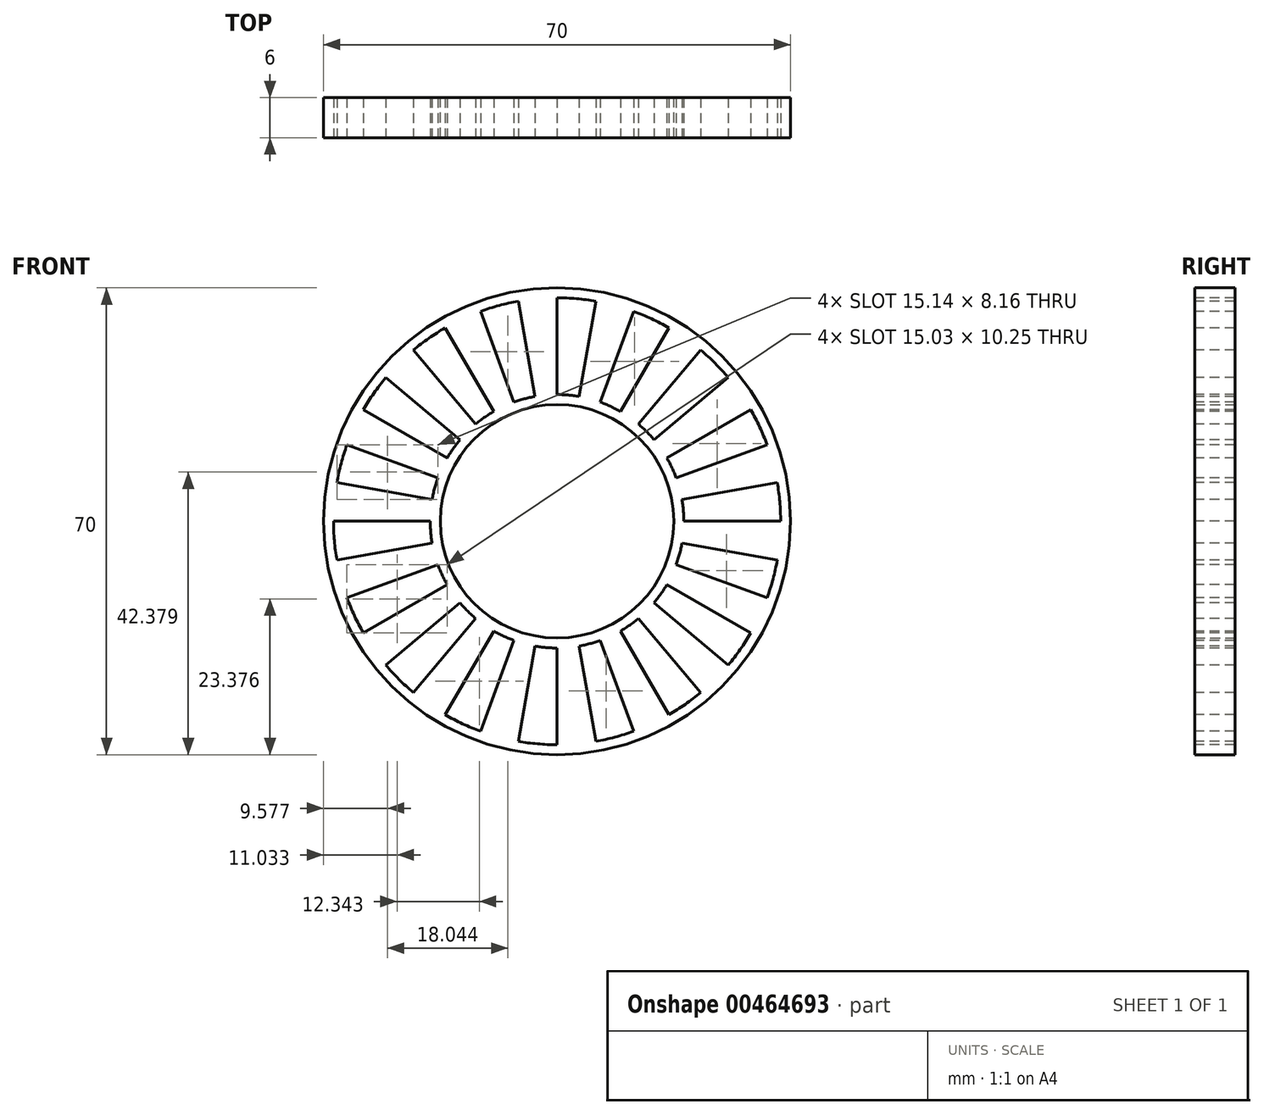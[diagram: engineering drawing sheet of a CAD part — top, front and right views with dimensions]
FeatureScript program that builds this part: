
annotation { "Feature Type Name" : "Feature", "Feature Type Description" : "" }
export const myFeature = defineFeature(function(context is Context, id is Id, definition is map)
    precondition{}
    {
        {
            var Q0;
            Q0=qCreatedBy(makeId("Front.planeOp"),FACE);
            var sketch = newSketch(context, id + "F0", { "sketchPlane" : qUnion([Q0])});
            skCircle(sketch, "E0", {"center": v(0, 0) * mm, "radius": 47.5 * mm, "construction": true});
            skCircle(sketch, "E1", {"center": v(0, 0) * mm, "radius": 35 * mm});
            skCircle(sketch, "E2", {"center": v(0, 0) * mm, "radius": 17.5 * mm});
            skSolve(sketch);
        }
        {
            var Q0;
            Q0=makeQuery(id+"F0.imprint","IMPRINT",FACE,{"disambiguationData":[TD([[makeQuery(id+"F0.imprint","IMPRINT",EDGE,{"derivedFrom":sQuery(id+"F0.wireOp",EDGE,"E1")}),1.0]])]});
            extrude(context, id + "F1", {"entities" : qUnion([Q0]), "depth" : 6 * mm});
        }
        {
            var Q0;
            Q0=makeQuery(id+"F1.opExtrude","CAP_FACE",FACE,{"disambiguationData":[OSD([sQuery(id+"F0.wireOp",EDGE,"E1"),sQuery(id+"F0.wireOp",EDGE,"E2")])],"isStart":false});
            var sketch = newSketch(context, id + "F2", { "sketchPlane" : qUnion([Q0])});
            skCircle(sketch, "E3.0", {"center": v(0, 0) * mm, "radius": 17.5 * mm, "construction": true});
            skCircle(sketch, "E4.0", {"center": v(0, 0) * mm, "radius": 35 * mm, "construction": true});
            skArc(sketch, "E5", {"start": v(3.3, 18.71) * mm, "mid": v(1.66, 18.93) * mm, "end": v(0, 19) * mm});
            skArc(sketch, "E6", {"start": v(5.82, 33) * mm, "mid": v(2.92, 33.37) * mm, "end": v(0, 33.5) * mm});
            skLineSegment(sketch, "E7", {"start": v(0, 19) * mm, "end": v(0, 33.5) * mm});
            skLineSegment(sketch, "E8.1.0", {"start": v(-3.3, 18.71) * mm, "end": v(-5.82, 33) * mm});
            skLineSegment(sketch, "E8.2.0", {"start": v(-6.5, 17.85) * mm, "end": v(-11.46, 31.48) * mm});
            skLineSegment(sketch, "E8.3.0", {"start": v(-9.5, 16.45) * mm, "end": v(-16.75, 29.01) * mm});
            skLineSegment(sketch, "E8.4.0", {"start": v(-12.21, 14.55) * mm, "end": v(-21.53, 25.66) * mm});
            skLineSegment(sketch, "E8.5.0", {"start": v(-14.55, 12.21) * mm, "end": v(-25.66, 21.53) * mm});
            skLineSegment(sketch, "E8.6.0", {"start": v(-16.45, 9.5) * mm, "end": v(-29.01, 16.75) * mm});
            skLineSegment(sketch, "E8.7.0", {"start": v(-17.85, 6.5) * mm, "end": v(-31.48, 11.46) * mm});
            skLineSegment(sketch, "E8.8.0", {"start": v(-18.71, 3.3) * mm, "end": v(-33, 5.82) * mm});
            skLineSegment(sketch, "E8.9.0", {"start": v(-19, 0) * mm, "end": v(-33.5, 0) * mm});
            skLineSegment(sketch, "E8.10.0", {"start": v(-18.71, -3.3) * mm, "end": v(-33, -5.82) * mm});
            skLineSegment(sketch, "E8.11.0", {"start": v(-17.85, -6.5) * mm, "end": v(-31.48, -11.46) * mm});
            skLineSegment(sketch, "E8.12.0", {"start": v(-16.45, -9.5) * mm, "end": v(-29.01, -16.75) * mm});
            skLineSegment(sketch, "E8.13.0", {"start": v(-14.55, -12.21) * mm, "end": v(-25.66, -21.53) * mm});
            skLineSegment(sketch, "E8.14.0", {"start": v(-12.21, -14.55) * mm, "end": v(-21.53, -25.66) * mm});
            skLineSegment(sketch, "E8.15.0", {"start": v(-9.5, -16.45) * mm, "end": v(-16.75, -29.01) * mm});
            skLineSegment(sketch, "E8.16.0", {"start": v(-6.5, -17.85) * mm, "end": v(-11.46, -31.48) * mm});
            skLineSegment(sketch, "E8.17.0", {"start": v(-3.3, -18.71) * mm, "end": v(-5.82, -33) * mm});
            skLineSegment(sketch, "E8.18.0", {"start": v(0, -19) * mm, "end": v(0, -33.5) * mm});
            skLineSegment(sketch, "E8.19.0", {"start": v(3.3, -18.71) * mm, "end": v(5.82, -33) * mm});
            skLineSegment(sketch, "E8.20.0", {"start": v(6.5, -17.85) * mm, "end": v(11.46, -31.48) * mm});
            skLineSegment(sketch, "E8.21.0", {"start": v(9.5, -16.45) * mm, "end": v(16.75, -29.01) * mm});
            skLineSegment(sketch, "E8.22.0", {"start": v(12.21, -14.55) * mm, "end": v(21.53, -25.66) * mm});
            skLineSegment(sketch, "E8.23.0", {"start": v(14.55, -12.21) * mm, "end": v(25.66, -21.53) * mm});
            skLineSegment(sketch, "E8.24.0", {"start": v(16.45, -9.5) * mm, "end": v(29.01, -16.75) * mm});
            skLineSegment(sketch, "E8.25.0", {"start": v(17.85, -6.5) * mm, "end": v(31.48, -11.46) * mm});
            skLineSegment(sketch, "E8.26.0", {"start": v(18.71, -3.3) * mm, "end": v(33, -5.82) * mm});
            skLineSegment(sketch, "E8.27.0", {"start": v(19, 0) * mm, "end": v(33.5, 0) * mm});
            skLineSegment(sketch, "E8.28.0", {"start": v(18.71, 3.3) * mm, "end": v(33, 5.82) * mm});
            skLineSegment(sketch, "E8.29.0", {"start": v(17.85, 6.5) * mm, "end": v(31.48, 11.46) * mm});
            skLineSegment(sketch, "E8.30.0", {"start": v(16.45, 9.5) * mm, "end": v(29.01, 16.75) * mm});
            skLineSegment(sketch, "E8.31.0", {"start": v(14.55, 12.21) * mm, "end": v(25.66, 21.53) * mm});
            skLineSegment(sketch, "E8.32.0", {"start": v(12.21, 14.55) * mm, "end": v(21.53, 25.66) * mm});
            skLineSegment(sketch, "E8.33.0", {"start": v(9.5, 16.45) * mm, "end": v(16.75, 29.01) * mm});
            skLineSegment(sketch, "E8.34.0", {"start": v(6.5, 17.85) * mm, "end": v(11.46, 31.48) * mm});
            skLineSegment(sketch, "E8.35.0", {"start": v(3.3, 18.71) * mm, "end": v(5.82, 33) * mm});
            skArc(sketch, "E9.trimOffspring", {"start": v(9.5, 16.45) * mm, "mid": v(8.03, 17.22) * mm, "end": v(6.5, 17.85) * mm});
            skArc(sketch, "E10.trimOffspring", {"start": v(16.75, 29.01) * mm, "mid": v(14.16, 30.36) * mm, "end": v(11.46, 31.48) * mm});
            skArc(sketch, "E11.trimOffspring", {"start": v(25.66, 21.53) * mm, "mid": v(23.69, 23.69) * mm, "end": v(21.53, 25.66) * mm});
            skArc(sketch, "E12.trimOffspring", {"start": v(14.55, 12.21) * mm, "mid": v(13.44, 13.44) * mm, "end": v(12.21, 14.55) * mm});
            skArc(sketch, "E13.trimOffspring", {"start": v(17.85, 6.5) * mm, "mid": v(17.22, 8.03) * mm, "end": v(16.45, 9.5) * mm});
            skArc(sketch, "E14.trimOffspring", {"start": v(31.48, 11.46) * mm, "mid": v(30.36, 14.16) * mm, "end": v(29.01, 16.75) * mm});
            skArc(sketch, "E15.trimOffspring", {"start": v(33.5, 0) * mm, "mid": v(33.37, 2.92) * mm, "end": v(33, 5.82) * mm});
            skArc(sketch, "E16.trimOffspring", {"start": v(19, 0) * mm, "mid": v(18.93, 1.66) * mm, "end": v(18.71, 3.3) * mm});
            skArc(sketch, "E17.trimOffspring", {"start": v(17.85, -6.5) * mm, "mid": v(18.35, -4.92) * mm, "end": v(18.71, -3.3) * mm});
            skArc(sketch, "E18.trimOffspring", {"start": v(31.48, -11.46) * mm, "mid": v(32.36, -8.67) * mm, "end": v(33, -5.82) * mm});
            skArc(sketch, "E19.trimOffspring", {"start": v(25.66, -21.53) * mm, "mid": v(27.44, -19.21) * mm, "end": v(29.01, -16.75) * mm});
            skArc(sketch, "E20.trimOffspring", {"start": v(14.55, -12.21) * mm, "mid": v(15.56, -10.9) * mm, "end": v(16.45, -9.5) * mm});
            skArc(sketch, "E21.trimOffspring", {"start": v(16.75, -29.01) * mm, "mid": v(19.21, -27.44) * mm, "end": v(21.53, -25.66) * mm});
            skArc(sketch, "E22.trimOffspring", {"start": v(9.5, -16.45) * mm, "mid": v(10.9, -15.56) * mm, "end": v(12.21, -14.55) * mm});
            skArc(sketch, "E23.trimOffspring", {"start": v(3.3, -18.71) * mm, "mid": v(4.92, -18.35) * mm, "end": v(6.5, -17.85) * mm});
            skArc(sketch, "E24.trimOffspring", {"start": v(5.82, -33) * mm, "mid": v(8.67, -32.36) * mm, "end": v(11.46, -31.48) * mm});
            skArc(sketch, "E25.trimOffspring", {"start": v(-5.82, -33) * mm, "mid": v(-2.92, -33.37) * mm, "end": v(0, -33.5) * mm});
            skArc(sketch, "E26.trimOffspring", {"start": v(-3.3, -18.71) * mm, "mid": v(-1.66, -18.93) * mm, "end": v(0, -19) * mm});
            skArc(sketch, "E27.trimOffspring", {"start": v(-9.5, -16.45) * mm, "mid": v(-8.03, -17.22) * mm, "end": v(-6.5, -17.85) * mm});
            skArc(sketch, "E28.trimOffspring", {"start": v(-16.75, -29.01) * mm, "mid": v(-14.16, -30.36) * mm, "end": v(-11.46, -31.48) * mm});
            skArc(sketch, "E29.trimOffspring", {"start": v(-25.66, -21.53) * mm, "mid": v(-23.69, -23.69) * mm, "end": v(-21.53, -25.66) * mm});
            skArc(sketch, "E30.trimOffspring", {"start": v(-14.55, -12.21) * mm, "mid": v(-13.44, -13.44) * mm, "end": v(-12.21, -14.55) * mm});
            skArc(sketch, "E31.trimOffspring", {"start": v(-17.85, -6.5) * mm, "mid": v(-17.22, -8.03) * mm, "end": v(-16.45, -9.5) * mm});
            skArc(sketch, "E32.trimOffspring", {"start": v(-31.48, -11.46) * mm, "mid": v(-30.36, -14.16) * mm, "end": v(-29.01, -16.75) * mm});
            skArc(sketch, "E33.trimOffspring", {"start": v(-19, 0) * mm, "mid": v(-18.93, -1.66) * mm, "end": v(-18.71, -3.3) * mm});
            skArc(sketch, "E34.trimOffspring", {"start": v(-33.5, 0) * mm, "mid": v(-33.37, -2.92) * mm, "end": v(-33, -5.82) * mm});
            skArc(sketch, "E35.trimOffspring", {"start": v(-17.85, 6.5) * mm, "mid": v(-18.35, 4.92) * mm, "end": v(-18.71, 3.3) * mm});
            skArc(sketch, "E36.trimOffspring", {"start": v(-31.48, 11.46) * mm, "mid": v(-32.36, 8.67) * mm, "end": v(-33, 5.82) * mm});
            skArc(sketch, "E37.trimOffspring", {"start": v(-14.55, 12.21) * mm, "mid": v(-15.56, 10.9) * mm, "end": v(-16.45, 9.5) * mm});
            skArc(sketch, "E38.trimOffspring", {"start": v(-25.66, 21.53) * mm, "mid": v(-27.44, 19.21) * mm, "end": v(-29.01, 16.75) * mm});
            skArc(sketch, "E39.trimOffspring", {"start": v(-9.5, 16.45) * mm, "mid": v(-10.9, 15.56) * mm, "end": v(-12.21, 14.55) * mm});
            skArc(sketch, "E40.trimOffspring", {"start": v(-16.75, 29.01) * mm, "mid": v(-19.21, 27.44) * mm, "end": v(-21.53, 25.66) * mm});
            skArc(sketch, "E41.trimOffspring", {"start": v(-5.82, 33) * mm, "mid": v(-8.67, 32.36) * mm, "end": v(-11.46, 31.48) * mm});
            skArc(sketch, "E42.trimOffspring", {"start": v(-3.3, 18.71) * mm, "mid": v(-4.92, 18.35) * mm, "end": v(-6.5, 17.85) * mm});
            skPoint(sketch, "E43.orphan", {"position": v(0, 35) * mm});
            skPoint(sketch, "E44.orphan", {"position": v(6.08, 34.47) * mm});
            skPoint(sketch, "E45.orphan", {"position": v(11.97, 32.89) * mm});
            skPoint(sketch, "E46.orphan", {"position": v(17.5, 30.31) * mm});
            skPoint(sketch, "E47.orphan", {"position": v(22.5, 26.81) * mm});
            skPoint(sketch, "E48.orphan", {"position": v(26.81, 22.5) * mm});
            skPoint(sketch, "E49.orphan", {"position": v(30.31, 17.5) * mm});
            skPoint(sketch, "E50.orphan", {"position": v(32.89, 11.97) * mm});
            skPoint(sketch, "E51.orphan", {"position": v(34.47, 6.08) * mm});
            skPoint(sketch, "E52.orphan", {"position": v(35, 0) * mm});
            skPoint(sketch, "E53.orphan", {"position": v(34.47, -6.08) * mm});
            skPoint(sketch, "E54.orphan", {"position": v(32.89, -11.97) * mm});
            skPoint(sketch, "E55.orphan", {"position": v(30.31, -17.5) * mm});
            skPoint(sketch, "E56.orphan", {"position": v(26.81, -22.5) * mm});
            skPoint(sketch, "E57.orphan", {"position": v(22.5, -26.81) * mm});
            skPoint(sketch, "E58.orphan", {"position": v(17.5, -30.31) * mm});
            skPoint(sketch, "E59.orphan", {"position": v(11.97, -32.89) * mm});
            skPoint(sketch, "E60.orphan", {"position": v(6.08, -34.47) * mm});
            skPoint(sketch, "E61.orphan", {"position": v(0, -35) * mm});
            skPoint(sketch, "E62.orphan", {"position": v(-6.08, -34.47) * mm});
            skPoint(sketch, "E63.orphan", {"position": v(-11.97, -32.89) * mm});
            skPoint(sketch, "E64.orphan", {"position": v(-17.5, -30.31) * mm});
            skPoint(sketch, "E65.orphan", {"position": v(-22.5, -26.81) * mm});
            skPoint(sketch, "E66.orphan", {"position": v(-26.81, -22.5) * mm});
            skPoint(sketch, "E67.orphan", {"position": v(-30.31, -17.5) * mm});
            skPoint(sketch, "E68.orphan", {"position": v(-32.89, -11.97) * mm});
            skPoint(sketch, "E69.orphan", {"position": v(-34.47, -6.08) * mm});
            skPoint(sketch, "E70.orphan", {"position": v(-35, 0) * mm});
            skPoint(sketch, "E71.orphan", {"position": v(-32.89, 11.97) * mm});
            skPoint(sketch, "E72.orphan", {"position": v(-34.47, 6.08) * mm});
            skPoint(sketch, "E73.orphan", {"position": v(-6.08, 34.47) * mm});
            skPoint(sketch, "E74.orphan", {"position": v(-11.97, 32.89) * mm});
            skPoint(sketch, "E75.orphan", {"position": v(-17.5, 30.31) * mm});
            skPoint(sketch, "E76.orphan", {"position": v(-22.5, 26.81) * mm});
            skPoint(sketch, "E77.orphan", {"position": v(-26.81, 22.5) * mm});
            skPoint(sketch, "E78.orphan", {"position": v(-30.31, 17.5) * mm});
            skSolve(sketch);
        }
        {
            var Q0;
            Q0=makeQuery(id+"F2.imprint","IMPRINT",FACE,{"disambiguationData":[TD([[makeQuery(id+"F2.imprint","IMPRINT",EDGE,{"derivedFrom":sQuery(id+"F2.wireOp",EDGE,"E8.23.0")}),1.0]])]});
            var Q1;
            Q1=makeQuery(id+"F2.imprint","IMPRINT",FACE,{"disambiguationData":[TD([[makeQuery(id+"F2.imprint","IMPRINT",EDGE,{"derivedFrom":sQuery(id+"F2.wireOp",EDGE,"E8.25.0")}),1.0]])]});
            var Q2;
            Q2=makeQuery(id+"F2.imprint","IMPRINT",FACE,{"disambiguationData":[TD([[makeQuery(id+"F2.imprint","IMPRINT",EDGE,{"derivedFrom":sQuery(id+"F2.wireOp",EDGE,"E8.27.0")}),1.0]])]});
            var Q3;
            Q3=makeQuery(id+"F2.imprint","IMPRINT",FACE,{"disambiguationData":[TD([[makeQuery(id+"F2.imprint","IMPRINT",EDGE,{"derivedFrom":sQuery(id+"F2.wireOp",EDGE,"E8.29.0")}),1.0]])]});
            var Q4;
            Q4=makeQuery(id+"F2.imprint","IMPRINT",FACE,{"disambiguationData":[TD([[makeQuery(id+"F2.imprint","IMPRINT",EDGE,{"derivedFrom":sQuery(id+"F2.wireOp",EDGE,"E8.33.0")}),1.0]])]});
            var Q5;
            Q5=makeQuery(id+"F2.imprint","IMPRINT",FACE,{"disambiguationData":[TD([[makeQuery(id+"F2.imprint","IMPRINT",EDGE,{"derivedFrom":sQuery(id+"F2.wireOp",EDGE,"E8.31.0")}),1.0]])]});
            var Q6;
            Q6=makeQuery(id+"F2.imprint","IMPRINT",FACE,{"disambiguationData":[TD([[makeQuery(id+"F2.imprint","IMPRINT",EDGE,{"derivedFrom":sQuery(id+"F2.wireOp",EDGE,"E5")}),-1.0]])]});
            var Q7;
            Q7=makeQuery(id+"F2.imprint","IMPRINT",FACE,{"disambiguationData":[TD([[makeQuery(id+"F2.imprint","IMPRINT",EDGE,{"derivedFrom":sQuery(id+"F2.wireOp",EDGE,"E8.1.0")}),1.0]])]});
            var Q8;
            Q8=makeQuery(id+"F2.imprint","IMPRINT",FACE,{"disambiguationData":[TD([[makeQuery(id+"F2.imprint","IMPRINT",EDGE,{"derivedFrom":sQuery(id+"F2.wireOp",EDGE,"E8.3.0")}),1.0]])]});
            var Q9;
            Q9=makeQuery(id+"F2.imprint","IMPRINT",FACE,{"disambiguationData":[TD([[makeQuery(id+"F2.imprint","IMPRINT",EDGE,{"derivedFrom":sQuery(id+"F2.wireOp",EDGE,"E8.5.0")}),1.0]])]});
            var Q10;
            Q10=makeQuery(id+"F2.imprint","IMPRINT",FACE,{"disambiguationData":[TD([[makeQuery(id+"F2.imprint","IMPRINT",EDGE,{"derivedFrom":sQuery(id+"F2.wireOp",EDGE,"E8.7.0")}),1.0]])]});
            var Q11;
            Q11=makeQuery(id+"F2.imprint","IMPRINT",FACE,{"disambiguationData":[TD([[makeQuery(id+"F2.imprint","IMPRINT",EDGE,{"derivedFrom":sQuery(id+"F2.wireOp",EDGE,"E8.13.0")}),1.0]])]});
            var Q12;
            Q12=makeQuery(id+"F2.imprint","IMPRINT",FACE,{"disambiguationData":[TD([[makeQuery(id+"F2.imprint","IMPRINT",EDGE,{"derivedFrom":sQuery(id+"F2.wireOp",EDGE,"E8.9.0")}),1.0]])]});
            var Q13;
            Q13=makeQuery(id+"F2.imprint","IMPRINT",FACE,{"disambiguationData":[TD([[makeQuery(id+"F2.imprint","IMPRINT",EDGE,{"derivedFrom":sQuery(id+"F2.wireOp",EDGE,"E8.11.0")}),1.0]])]});
            var Q14;
            Q14=makeQuery(id+"F2.imprint","IMPRINT",FACE,{"disambiguationData":[TD([[makeQuery(id+"F2.imprint","IMPRINT",EDGE,{"derivedFrom":sQuery(id+"F2.wireOp",EDGE,"E8.17.0")}),1.0]])]});
            var Q15;
            Q15=makeQuery(id+"F2.imprint","IMPRINT",FACE,{"disambiguationData":[TD([[makeQuery(id+"F2.imprint","IMPRINT",EDGE,{"derivedFrom":sQuery(id+"F2.wireOp",EDGE,"E8.15.0")}),1.0]])]});
            var Q16;
            Q16=makeQuery(id+"F2.imprint","IMPRINT",FACE,{"disambiguationData":[TD([[makeQuery(id+"F2.imprint","IMPRINT",EDGE,{"derivedFrom":sQuery(id+"F2.wireOp",EDGE,"E8.19.0")}),1.0]])]});
            var Q17;
            Q17=makeQuery(id+"F2.imprint","IMPRINT",FACE,{"disambiguationData":[TD([[makeQuery(id+"F2.imprint","IMPRINT",EDGE,{"derivedFrom":sQuery(id+"F2.wireOp",EDGE,"E8.21.0")}),1.0]])]});
            extrude(context, id + "F3", {"entities" : qUnion([Q0, Q1, Q2, Q3, Q4, Q5, Q6, Q7, Q8, Q9, Q10, Q11, Q12, Q13, Q14, Q15, Q16, Q17]), "operationType" : NewBodyOperationType.REMOVE, "endBound" : BoundingType.THROUGH_ALL, "oppositeDirection" : true, "depth" : 25 * mm});
        }
    });
